# Revit family: BE_77953_de_DE
name_source: partatom
category: Leuchten
revit_build: Autodesk Revit 2015 (Build: 20160512_0715(x64)
units: mm (PartAtom-declared; Revit-internal decimal feet)

## types (1)
- BE_77953_de_DE
    BEGA_Dummy = Nein
    BEGA_IES = Ja
    BEGA_IES1 = Ja
    BEGA_IES2 = Ja
    BEGA_IES3 = Ja
    BEGA_IES_X1 = 0 mm  [stored 0 ft]
    BEGA_IES_X2 = 0 mm  [stored 0 ft]
    BEGA_IES_Y1 = 0 mm  [stored 0 ft]
    BEGA_IES_Y2 = 0 mm  [stored 0 ft]
    BEGA_IES_Z1 = 0 mm  [stored 0 ft]
    BEGA_IES_Z2 = 0 mm  [stored 0 ft]
    BEGA_Intern = Ja
    BEGA_Intern_Konstruktion = Ja
    BEGA_Intern_an = Ja
    BEGA_Intern_aus = Ja
    Hersteller = BEGA
    Lastklassifizierung = Beleuchtung
    Logo = <Keine Auswahl>
    M_A = Ja
    M_G = Ja
    M_W = Ja
    Material_02 = BEGA_Oberfläche_Silber_matt
    Material_03 = BEGA_Oberfläche_Weiss_matt
    Material_06 = BEGA_Oberfläche_Edelstahl_gebürstet
    Material_09 = BEGA_Glas_klar
    Material_11 = BEGA_Glas_opal
    Material_15 = BEGA_Leuchtmedium_matt
    Material_17 = BEGA_Reflektor
    Scheinlast = 0 VA
    Sonderanfertigung = Nein
    Spannung = 0 V
    URL = http://www.bega.de
    Vorgabe-Ansicht = 0 mm  [stored 0 ft]

note: [stored X ft] marks values corroborated as IEEE doubles in the binary element streams (Revit-internal decimal feet)
